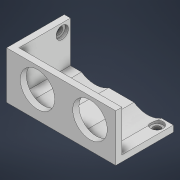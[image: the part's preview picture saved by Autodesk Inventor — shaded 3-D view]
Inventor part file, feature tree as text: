
AUTODESK INVENTOR PART (.ipt)
format: ipt  version: 2022 (Build 260153000, 153)  size: 163,840 bytes
history: native  units: mm
features: sketch x5, extrude x3, hole x2, projected_geometry x1
ambient origin geometry x8: Origin, YZ Plane, XZ Plane, XY Plane, X Axis, Y Axis, Z Axis, Center Point
bodies: Volumenkörper1 (feature_tree)
feature tree (11):
  extrude  "Extrusion1"  Depth=15.0mm
  extrude  "Extrusion2"  Depth=3.0mm TaperAngle=0.0deg
  hole  "Bohrung1"  [1 undecoded]
  hole  "Bohrung2"  [1 undecoded]
  extrude  "Extrusion3"  Depth=4.0mm
  sketch  "Skizze1"  dims[d1=16.75mm d5=15.0mm]
  sketch  "Skizze2"  dims[d7=10.0mm d8=3.0mm d9=0.0mm]
  projected_geometry  "Projizierte Kontur1"
  sketch  "Skizze3"  dims[d11=3.0mm d12=25.0mm d13=0.0mm]
  sketch  "Skizze4"  dims[d14=12.5mm]
  sketch  "Skizze5"  dims[d15=3.5mm d16=6.0mm d17=6.0mm d18=1.5mm d19=90.0deg d20=8.0mm d21=20.594885mm d22=4.0mm d23=4.0mm d24=3.5mm d25=6.0mm d26=6.0mm d27=1.5mm d28=90.0deg d29=8.0mm d30=20.594885mm d31=4.0mm d32=4.0mm d33=24.0mm d34=24.0mm d35=25.0mm d36=0.0mm]
note: 2 required parameter values undecoded (feature->parameter linkage not recoverable at this tier; creation-order binding heuristic only, values carry confidence <= 0.55)
